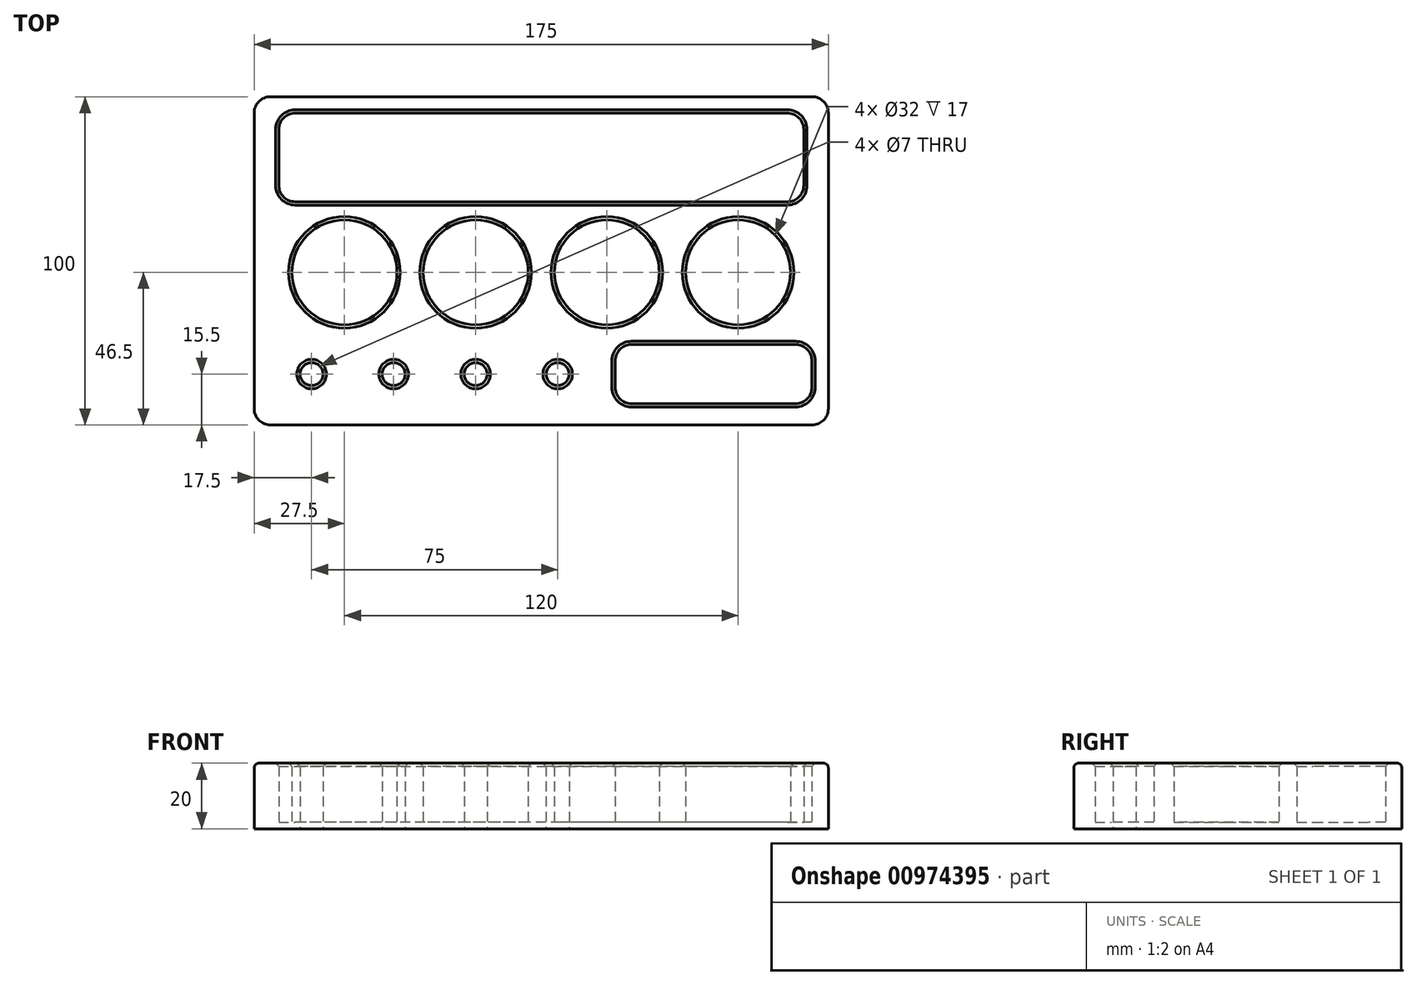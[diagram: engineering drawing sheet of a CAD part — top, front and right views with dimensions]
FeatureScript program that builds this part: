
annotation { "Feature Type Name" : "Feature", "Feature Type Description" : "" }
export const myFeature = defineFeature(function(context is Context, id is Id, definition is map)
    precondition{}
    {
        {
            var Q0;
            Q0=qCreatedBy(makeId("Top.planeOp"),FACE);
            var sketch = newSketch(context, id + "F0", { "sketchPlane" : qUnion([Q0])});
            skLineSegment(sketch, "E0.bottom", {"start": v(-82.5, 50) * mm, "end": v(82.5, 50) * mm});
            skLineSegment(sketch, "E0.top", {"start": v(-82.5, -50) * mm, "end": v(82.5, -50) * mm});
            skLineSegment(sketch, "E0.left", {"start": v(-87.5, 45) * mm, "end": v(-87.5, -45) * mm});
            skLineSegment(sketch, "E0.right", {"start": v(87.5, 45) * mm, "end": v(87.5, -45) * mm});
            skPoint(sketch, "E0.middle", {"position": v(0, 0) * mm});
            skCircle(sketch, "E1", {"center": v(-60, -3.5) * mm, "radius": 16 * mm});
            skCircle(sketch, "E2", {"center": v(-20, -3.5) * mm, "radius": 16 * mm});
            skCircle(sketch, "E3", {"center": v(60, -3.5) * mm, "radius": 16 * mm});
            skCircle(sketch, "E4", {"center": v(-70, -34.5) * mm, "radius": 12.5 * mm});
            skCircle(sketch, "E5", {"center": v(-70, -34.5) * mm, "radius": 3.5 * mm});
            skCircle(sketch, "E6", {"center": v(-45, -34.5) * mm, "radius": 12.5 * mm});
            skCircle(sketch, "E7", {"center": v(-45, -34.5) * mm, "radius": 3.5 * mm});
            skCircle(sketch, "E8", {"center": v(-20, -34.5) * mm, "radius": 12.5 * mm});
            skCircle(sketch, "E9", {"center": v(-20, -34.5) * mm, "radius": 3.5 * mm});
            skCircle(sketch, "E10", {"center": v(5, -34.5) * mm, "radius": 12.5 * mm});
            skCircle(sketch, "E11", {"center": v(5, -34.5) * mm, "radius": 3.5 * mm});
            skPoint(sketch, "E12.visualSharp", {"position": v(-87.5, 50) * mm});
            skArc(sketch, "E12.filletArc", {"start": v(-82.5, 50) * mm, "mid": v(-86.04, 48.54) * mm, "end": v(-87.5, 45) * mm});
            skPoint(sketch, "E13.visualSharp", {"position": v(87.5, 50) * mm});
            skArc(sketch, "E13.filletArc", {"start": v(87.5, 45) * mm, "mid": v(86.04, 48.54) * mm, "end": v(82.5, 50) * mm});
            skPoint(sketch, "E14.visualSharp", {"position": v(87.5, -50) * mm});
            skArc(sketch, "E14.filletArc", {"start": v(82.5, -50) * mm, "mid": v(86.04, -48.54) * mm, "end": v(87.5, -45) * mm});
            skPoint(sketch, "E15.visualSharp", {"position": v(-87.5, -50) * mm});
            skArc(sketch, "E15.filletArc", {"start": v(-87.5, -45) * mm, "mid": v(-86.04, -48.54) * mm, "end": v(-82.5, -50) * mm});
            skLineSegment(sketch, "E16.bottom", {"start": v(75, 18) * mm, "end": v(-75, 18) * mm});
            skLineSegment(sketch, "E16.top", {"start": v(75, 45) * mm, "end": v(-75, 45) * mm});
            skLineSegment(sketch, "E16.left", {"start": v(80, 23) * mm, "end": v(80, 40) * mm});
            skLineSegment(sketch, "E16.right", {"start": v(-80, 23) * mm, "end": v(-80, 40) * mm});
            skPoint(sketch, "E16.middle", {"position": v(0, 31.5) * mm});
            skLineSegment(sketch, "E17.bottom", {"start": v(77.5, -25.5) * mm, "end": v(27.5, -25.5) * mm});
            skLineSegment(sketch, "E17.top", {"start": v(77.5, -43.5) * mm, "end": v(27.5, -43.5) * mm});
            skLineSegment(sketch, "E17.left", {"start": v(82.5, -30.5) * mm, "end": v(82.5, -38.5) * mm});
            skLineSegment(sketch, "E17.right", {"start": v(22.5, -30.5) * mm, "end": v(22.5, -38.5) * mm});
            skPoint(sketch, "E17.middle", {"position": v(52.5, -34.5) * mm});
            skPoint(sketch, "E18.visualSharp", {"position": v(22.5, -25.5) * mm});
            skArc(sketch, "E18.filletArc", {"start": v(27.5, -25.5) * mm, "mid": v(23.96, -26.96) * mm, "end": v(22.5, -30.5) * mm});
            skPoint(sketch, "E19.visualSharp", {"position": v(22.5, -43.5) * mm});
            skArc(sketch, "E19.filletArc", {"start": v(22.5, -38.5) * mm, "mid": v(23.96, -42.04) * mm, "end": v(27.5, -43.5) * mm});
            skPoint(sketch, "E20.visualSharp", {"position": v(82.5, -25.5) * mm});
            skArc(sketch, "E20.filletArc", {"start": v(82.5, -30.5) * mm, "mid": v(81.04, -26.96) * mm, "end": v(77.5, -25.5) * mm});
            skPoint(sketch, "E21.visualSharp", {"position": v(82.5, -43.5) * mm});
            skArc(sketch, "E21.filletArc", {"start": v(77.5, -43.5) * mm, "mid": v(81.04, -42.04) * mm, "end": v(82.5, -38.5) * mm});
            skPoint(sketch, "E22.visualSharp", {"position": v(80, 45) * mm});
            skArc(sketch, "E22.filletArc", {"start": v(80, 40) * mm, "mid": v(78.54, 43.54) * mm, "end": v(75, 45) * mm});
            skPoint(sketch, "E23.visualSharp", {"position": v(80, 18) * mm});
            skArc(sketch, "E23.filletArc", {"start": v(75, 18) * mm, "mid": v(78.54, 19.46) * mm, "end": v(80, 23) * mm});
            skPoint(sketch, "E24.visualSharp", {"position": v(-80, 18) * mm});
            skArc(sketch, "E24.filletArc", {"start": v(-80, 23) * mm, "mid": v(-78.54, 19.46) * mm, "end": v(-75, 18) * mm});
            skPoint(sketch, "E25.visualSharp", {"position": v(-80, 45) * mm});
            skArc(sketch, "E25.filletArc", {"start": v(-75, 45) * mm, "mid": v(-78.54, 43.54) * mm, "end": v(-80, 40) * mm});
            skLineSegment(sketch, "E26.0", {"start": v(75, 16) * mm, "end": v(-75, 16) * mm});
            skArc(sketch, "E27.0", {"start": v(-82, 23) * mm, "mid": v(-79.95, 18.05) * mm, "end": v(-75, 16) * mm});
            skLineSegment(sketch, "E28.0", {"start": v(-82, 23) * mm, "end": v(-82, 40) * mm});
            skArc(sketch, "E29.0", {"start": v(-75, 47) * mm, "mid": v(-79.95, 44.95) * mm, "end": v(-82, 40) * mm});
            skLineSegment(sketch, "E30.0", {"start": v(75, 47) * mm, "end": v(-75, 47) * mm});
            skArc(sketch, "E31.0", {"start": v(82, 40) * mm, "mid": v(79.95, 44.95) * mm, "end": v(75, 47) * mm});
            skLineSegment(sketch, "E32.0", {"start": v(82, 23) * mm, "end": v(82, 40) * mm});
            skArc(sketch, "E33.0", {"start": v(75, 16) * mm, "mid": v(79.95, 18.05) * mm, "end": v(82, 23) * mm});
            skCircle(sketch, "E34.0", {"center": v(60, -3.5) * mm, "radius": 18 * mm});
            skCircle(sketch, "E35.0", {"center": v(-20, -3.5) * mm, "radius": 18 * mm});
            skCircle(sketch, "E36.0", {"center": v(-60, -3.5) * mm, "radius": 18 * mm});
            skArc(sketch, "E37.0", {"start": v(27.5, -23.5) * mm, "mid": v(22.55, -25.55) * mm, "end": v(20.5, -30.5) * mm});
            skLineSegment(sketch, "E38.0", {"start": v(20.5, -30.5) * mm, "end": v(20.5, -38.5) * mm});
            skArc(sketch, "E39.0", {"start": v(20.5, -38.5) * mm, "mid": v(22.55, -43.45) * mm, "end": v(27.5, -45.5) * mm});
            skLineSegment(sketch, "E40.0", {"start": v(77.5, -45.5) * mm, "end": v(27.5, -45.5) * mm});
            skArc(sketch, "E41.0", {"start": v(77.5, -45.5) * mm, "mid": v(82.45, -43.45) * mm, "end": v(84.5, -38.5) * mm});
            skLineSegment(sketch, "E42.0", {"start": v(84.5, -30.5) * mm, "end": v(84.5, -38.5) * mm});
            skArc(sketch, "E43.0", {"start": v(84.5, -30.5) * mm, "mid": v(82.45, -25.55) * mm, "end": v(77.5, -23.5) * mm});
            skLineSegment(sketch, "E44.0", {"start": v(77.5, -23.5) * mm, "end": v(27.5, -23.5) * mm});
            skCircle(sketch, "E45", {"center": v(20, -3.5) * mm, "radius": 16 * mm});
            skCircle(sketch, "E46.0", {"center": v(20, -3.5) * mm, "radius": 18 * mm});
            skCircle(sketch, "E47.0", {"center": v(5, -34.5) * mm, "radius": 8.5 * mm});
            skCircle(sketch, "E48.0", {"center": v(-20, -34.5) * mm, "radius": 8.5 * mm});
            skCircle(sketch, "E49.0", {"center": v(-45, -34.5) * mm, "radius": 8.5 * mm});
            skCircle(sketch, "E50.0", {"center": v(-70, -34.5) * mm, "radius": 8.5 * mm});
            skSolve(sketch);
        }
        {
            var Q0;
            Q0=makeQuery(id+"F0.imprint","IMPRINT",FACE,{"disambiguationData":[TD([[makeQuery(id+"F0.imprint","IMPRINT",EDGE,{"derivedFrom":sQuery(id+"F0.wireOp",EDGE,"E0.bottom")}),-1.0]])]});
            var Q1;
            Q1=makeQuery(id+"F0.imprint","IMPRINT",FACE,{"disambiguationData":[TD([[makeQuery(id+"F0.imprint","IMPRINT",EDGE,{"derivedFrom":sQuery(id+"F0.wireOp",EDGE,"E16.bottom")}),1.0]])]});
            var Q2;
            Q2=makeQuery(id+"F0.imprint","IMPRINT",FACE,{"disambiguationData":[TD([[makeQuery(id+"F0.imprint","IMPRINT",EDGE,{"derivedFrom":sQuery(id+"F0.wireOp",EDGE,"E3")}),-1.0]])]});
            var Q3;
            Q3=makeQuery(id+"F0.imprint","IMPRINT",FACE,{"disambiguationData":[TD([[makeQuery(id+"F0.imprint","IMPRINT",EDGE,{"derivedFrom":sQuery(id+"F0.wireOp",EDGE,"E45")}),-1.0]])]});
            var Q4;
            Q4=makeQuery(id+"F0.imprint","IMPRINT",FACE,{"disambiguationData":[TD([[makeQuery(id+"F0.imprint","IMPRINT",EDGE,{"derivedFrom":sQuery(id+"F0.wireOp",EDGE,"E2")}),-1.0]])]});
            var Q5;
            Q5=makeQuery(id+"F0.imprint","IMPRINT",FACE,{"disambiguationData":[TD([[makeQuery(id+"F0.imprint","IMPRINT",EDGE,{"derivedFrom":sQuery(id+"F0.wireOp",EDGE,"E1")}),-1.0]])]});
            var Q6;
            Q6=makeQuery(id+"F0.imprint","IMPRINT",FACE,{"disambiguationData":[TD([[makeQuery(id+"F0.imprint","IMPRINT",EDGE,{"derivedFrom":sQuery(id+"F0.wireOp",EDGE,"E4")}),1.0]])]});
            var Q7;
            Q7=makeQuery(id+"F0.imprint","IMPRINT",FACE,{"disambiguationData":[TD([[makeQuery(id+"F0.imprint","IMPRINT",EDGE,{"derivedFrom":sQuery(id+"F0.wireOp",EDGE,"E5")}),-1.0]])]});
            var Q8;
            Q8=makeQuery(id+"F0.imprint","IMPRINT",FACE,{"disambiguationData":[TD([[makeQuery(id+"F0.imprint","IMPRINT",EDGE,{"derivedFrom":sQuery(id+"F0.wireOp",EDGE,"E49.0")}),-1.0]])]});
            var Q9;
            Q9=makeQuery(id+"F0.imprint","IMPRINT",FACE,{"disambiguationData":[TD([[makeQuery(id+"F0.imprint","IMPRINT",EDGE,{"derivedFrom":sQuery(id+"F0.wireOp",EDGE,"E7")}),-1.0]])]});
            var Q10;
            Q10=makeQuery(id+"F0.imprint","IMPRINT",FACE,{"disambiguationData":[TD([[makeQuery(id+"F0.imprint","IMPRINT",EDGE,{"derivedFrom":sQuery(id+"F0.wireOp",EDGE,"E48.0")}),-1.0]])]});
            var Q11;
            Q11=makeQuery(id+"F0.imprint","IMPRINT",FACE,{"disambiguationData":[TD([[makeQuery(id+"F0.imprint","IMPRINT",EDGE,{"derivedFrom":sQuery(id+"F0.wireOp",EDGE,"E9")}),-1.0]])]});
            var Q12;
            Q12=makeQuery(id+"F0.imprint","IMPRINT",FACE,{"disambiguationData":[TD([[makeQuery(id+"F0.imprint","IMPRINT",EDGE,{"derivedFrom":sQuery(id+"F0.wireOp",EDGE,"E10")}),1.0]])]});
            var Q13;
            Q13=makeQuery(id+"F0.imprint","IMPRINT",FACE,{"disambiguationData":[TD([[makeQuery(id+"F0.imprint","IMPRINT",EDGE,{"derivedFrom":sQuery(id+"F0.wireOp",EDGE,"E11")}),-1.0]])]});
            var Q14;
            Q14=makeQuery(id+"F0.imprint","IMPRINT",FACE,{"disambiguationData":[TD([[makeQuery(id+"F0.imprint","IMPRINT",EDGE,{"derivedFrom":sQuery(id+"F0.wireOp",EDGE,"E17.bottom")}),-1.0]])]});
            extrude(context, id + "F1", {"entities" : qUnion([Q0, Q1, Q2, Q3, Q4, Q5, Q6, Q7, Q8, Q9, Q10, Q11, Q12, Q13, Q14]), "depth" : 20 * mm, "offsetDistance" : 25 * mm});
        }
        {
            var Q0;
            Q0=makeQuery(id+"F0.imprint","IMPRINT",FACE,{"disambiguationData":[TD([[makeQuery(id+"F0.imprint","IMPRINT",EDGE,{"derivedFrom":sQuery(id+"F0.wireOp",EDGE,"E1")}),1.0]])]});
            var Q1;
            Q1=makeQuery(id+"F0.imprint","IMPRINT",FACE,{"disambiguationData":[TD([[makeQuery(id+"F0.imprint","IMPRINT",EDGE,{"derivedFrom":sQuery(id+"F0.wireOp",EDGE,"E2")}),1.0]])]});
            var Q2;
            Q2=makeQuery(id+"F0.imprint","IMPRINT",FACE,{"disambiguationData":[TD([[makeQuery(id+"F0.imprint","IMPRINT",EDGE,{"derivedFrom":sQuery(id+"F0.wireOp",EDGE,"57e835c9-7bf3-4cbb-8a98-6ba75118dbad")}),1.0]])]});
            var Q3;
            Q3=makeQuery(id+"F0.imprint","IMPRINT",FACE,{"disambiguationData":[TD([[makeQuery(id+"F0.imprint","IMPRINT",EDGE,{"derivedFrom":sQuery(id+"F0.wireOp",EDGE,"E3")}),1.0]])]});
            var Q4;
            Q4=makeQuery(id+"F0.imprint","IMPRINT",FACE,{"disambiguationData":[TD([[makeQuery(id+"F0.imprint","IMPRINT",EDGE,{"derivedFrom":sQuery(id+"F0.wireOp",EDGE,"453e4dce-1e40-4aee-ada9-6de44c946658")}),1.0]])]});
            var Q5;
            Q5=makeQuery(id+"F0.imprint","IMPRINT",FACE,{"disambiguationData":[TD([[makeQuery(id+"F0.imprint","IMPRINT",EDGE,{"derivedFrom":sQuery(id+"F0.wireOp",EDGE,"E16.bottom")}),-1.0]])]});
            var Q6;
            Q6=makeQuery(id+"F0.imprint","IMPRINT",FACE,{"disambiguationData":[TD([[makeQuery(id+"F0.imprint","IMPRINT",EDGE,{"derivedFrom":sQuery(id+"F0.wireOp",EDGE,"E17.bottom")}),1.0]])]});
            var Q7;
            Q7=makeQuery(id+"F0.imprint","IMPRINT",FACE,{"disambiguationData":[TD([[makeQuery(id+"F0.imprint","IMPRINT",EDGE,{"derivedFrom":sQuery(id+"F0.wireOp",EDGE,"E45")}),1.0]])]});
            extrude(context, id + "F2", {"entities" : qUnion([Q0, Q1, Q2, Q3, Q4, Q5, Q6, Q7]), "operationType" : NewBodyOperationType.ADD, "depth" : 2 * mm, "offsetDistance" : 25 * mm});
        }
        {
            var Q0;
            Q0=makeQuery(id+"F1.opExtrude","CAP_EDGE",EDGE,{"disambiguationData":[OSD([sQuery(id+"F0.wireOp",EDGE,"E0.top")])],"isStart":false});
            fillet(context, id + "F3", {"entities" : qUnion([Q0]), "radius" : 1.5 * mm, "tangentPropagation" : true, "allowEdgeOverflow" : false});
        }
        {
            var Q0;
            Q0=makeQuery(id+"F1.opExtrude","CAP_EDGE",EDGE,{"disambiguationData":[OSD([sQuery(id+"F0.wireOp",EDGE,"E1")])],"isStart":false});
            var Q1;
            Q1=makeQuery(id+"F1.opExtrude","CAP_EDGE",EDGE,{"disambiguationData":[OSD([sQuery(id+"F0.wireOp",EDGE,"E2")])],"isStart":false});
            var Q2;
            Q2=makeQuery(id+"F1.opExtrude","CAP_EDGE",EDGE,{"disambiguationData":[OSD([sQuery(id+"F0.wireOp",EDGE,"57e835c9-7bf3-4cbb-8a98-6ba75118dbad")])],"isStart":false});
            var Q3;
            Q3=makeQuery(id+"F1.opExtrude","CAP_EDGE",EDGE,{"disambiguationData":[OSD([sQuery(id+"F0.wireOp",EDGE,"E3")])],"isStart":false});
            var Q4;
            Q4=makeQuery(id+"F1.opExtrude","CAP_EDGE",EDGE,{"disambiguationData":[OSD([sQuery(id+"F0.wireOp",EDGE,"453e4dce-1e40-4aee-ada9-6de44c946658")])],"isStart":false});
            var Q5;
            Q5=makeQuery(id+"F1.opExtrude","CAP_EDGE",EDGE,{"disambiguationData":[OSD([sQuery(id+"F0.wireOp",EDGE,"E25.filletArc")])],"isStart":false});
            var Q6;
            Q6=makeQuery(id+"F1.opExtrude","CAP_EDGE",EDGE,{"disambiguationData":[OSD([sQuery(id+"F0.wireOp",EDGE,"E16.right")])],"isStart":false});
            var Q7;
            Q7=makeQuery(id+"F1.opExtrude","SWEPT_EDGE",EDGE,{"disambiguationData":[OSD([sQuery(id+"F0.wireOp",EDGE,"E17.right"),sQuery(id+"F0.wireOp",EDGE,"E18.filletArc")])]});
            var Q8;
            Q8=makeQuery(id+"F1.opExtrude","CAP_EDGE",EDGE,{"disambiguationData":[OSD([sQuery(id+"F0.wireOp",EDGE,"E18.filletArc")])],"isStart":false});
            var Q9;
            Q9=makeQuery(id+"F1.opExtrude","CAP_EDGE",EDGE,{"disambiguationData":[OSD([sQuery(id+"F0.wireOp",EDGE,"E45")])],"isStart":false});
            chamfer(context, id + "F4", {"entities" : qUnion([Q0, Q1, Q2, Q3, Q4, Q5, Q6, Q7, Q8, Q9]), "width" : 1 * mm, "tangentPropagation" : true});
        }
        {
            var Q0;
            Q0=makeQuery(id+"F1.opExtrude","CAP_EDGE",EDGE,{"disambiguationData":[OSD([sQuery(id+"F0.wireOp",EDGE,"E5")])],"isStart":false});
            var Q1;
            Q1=makeQuery(id+"F1.opExtrude","CAP_EDGE",EDGE,{"disambiguationData":[OSD([sQuery(id+"F0.wireOp",EDGE,"E7")])],"isStart":false});
            var Q2;
            Q2=makeQuery(id+"F1.opExtrude","CAP_EDGE",EDGE,{"disambiguationData":[OSD([sQuery(id+"F0.wireOp",EDGE,"E9")])],"isStart":false});
            var Q3;
            Q3=makeQuery(id+"F1.opExtrude","CAP_EDGE",EDGE,{"disambiguationData":[OSD([sQuery(id+"F0.wireOp",EDGE,"E11")])],"isStart":false});
            chamfer(context, id + "F5", {"entities" : qUnion([Q0, Q1, Q2, Q3]), "width" : 1 * mm, "tangentPropagation" : true});
        }
    });
